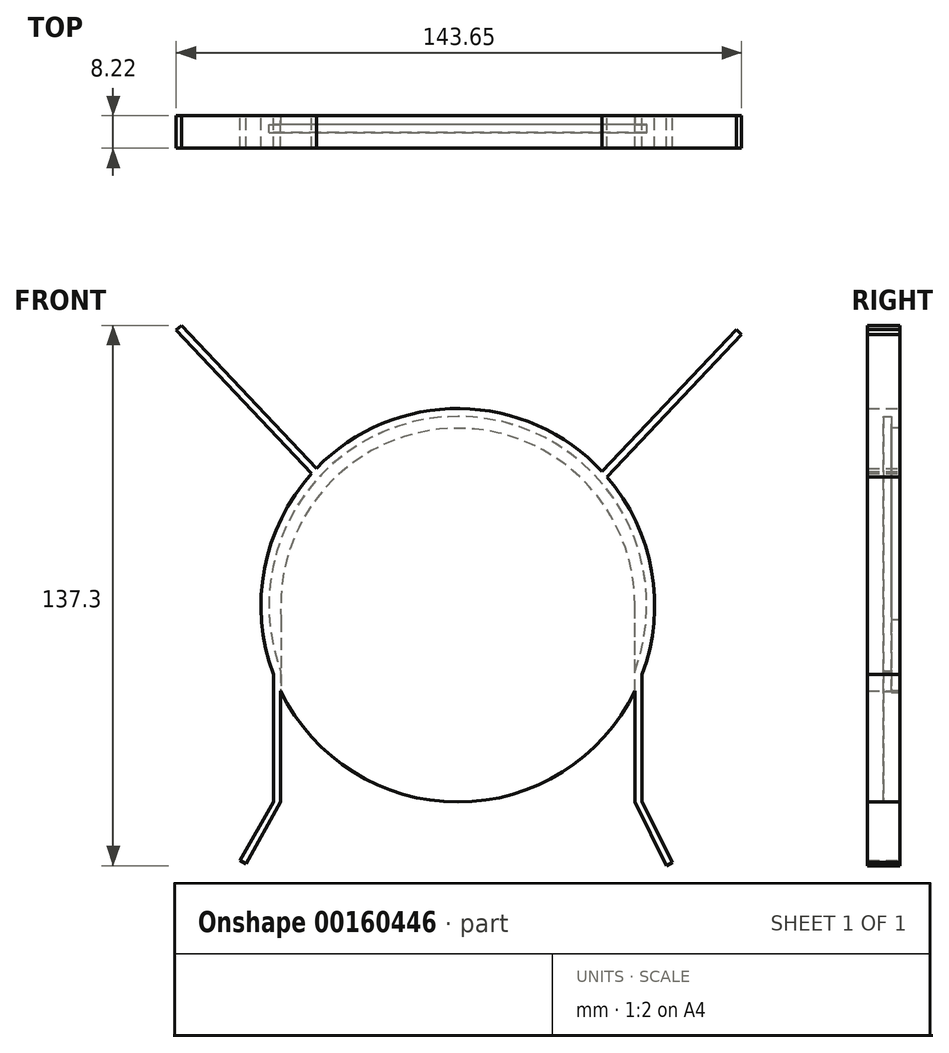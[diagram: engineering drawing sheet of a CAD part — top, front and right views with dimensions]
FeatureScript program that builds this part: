
annotation { "Feature Type Name" : "Feature", "Feature Type Description" : "" }
export const myFeature = defineFeature(function(context is Context, id is Id, definition is map)
    precondition{}
    {
        {
            var Q0;
            Q0=qCreatedBy(makeId("Front.planeOp"),FACE);
            var sketch = newSketch(context, id + "F0", { "sketchPlane" : qUnion([Q0])});
            skLineSegment(sketch, "E0", {"start": v(-45, 0) * mm, "end": v(-45, -50) * mm});
            skLineSegment(sketch, "E1", {"start": v(-45, -50) * mm, "end": v(-46.8, -50) * mm});
            skLineSegment(sketch, "E2", {"start": v(-46.8, -50) * mm, "end": v(-46.8, 0) * mm});
            skLineSegment(sketch, "E3", {"start": v(-46.8, 0) * mm, "end": v(-45, 0) * mm});
            skLineSegment(sketch, "E4", {"start": v(45, 0) * mm, "end": v(45, -50) * mm});
            skLineSegment(sketch, "E5", {"start": v(45, -50) * mm, "end": v(46.8, -50) * mm});
            skLineSegment(sketch, "E6", {"start": v(46.8, -50) * mm, "end": v(46.8, 0) * mm});
            skLineSegment(sketch, "E7", {"start": v(46.8, 0) * mm, "end": v(45, 0) * mm});
            skCircle(sketch, "E8", {"center": v(0, 0) * mm, "radius": 50 * mm});
            skLineSegment(sketch, "E9", {"start": v(-37.12, 33.5) * mm, "end": v(-71.54, 69.91) * mm});
            skLineSegment(sketch, "E10", {"start": v(-71.54, 69.91) * mm, "end": v(-70.23, 71.15) * mm});
            skLineSegment(sketch, "E11", {"start": v(-70.23, 71.15) * mm, "end": v(-35.89, 34.82) * mm});
            skLineSegment(sketch, "E12", {"start": v(36.69, 33.97) * mm, "end": v(70.8, 70.07) * mm});
            skLineSegment(sketch, "E13", {"start": v(70.8, 70.07) * mm, "end": v(72.1, 68.83) * mm});
            skLineSegment(sketch, "E14", {"start": v(72.1, 68.83) * mm, "end": v(37.77, 32.5) * mm});
            skLineSegment(sketch, "E15", {"start": v(-46.8, -50) * mm, "end": v(-55.36, -64.8) * mm});
            skLineSegment(sketch, "E16", {"start": v(-55.36, -64.8) * mm, "end": v(-53.8, -65.7) * mm});
            skLineSegment(sketch, "E17", {"start": v(-53.8, -65.7) * mm, "end": v(-45, -50) * mm});
            skLineSegment(sketch, "E18", {"start": v(45, -50) * mm, "end": v(52.95, -66.15) * mm});
            skLineSegment(sketch, "E19", {"start": v(52.95, -66.15) * mm, "end": v(54.56, -65.36) * mm});
            skLineSegment(sketch, "E20", {"start": v(54.56, -65.36) * mm, "end": v(46.8, -50) * mm});
            skSolve(sketch);
        }
        {
            var Q0;
            Q0=qCreatedBy(makeId("Front.planeOp"),FACE);
            var sketch = newSketch(context, id + "F1", { "sketchPlane" : qUnion([Q0])});
            skSolve(sketch);
        }
        {
            var Q0;
            Q0 = qSketchRegion(id + "F1", true);
            var Q1;
            {var subQ0=sQuery(id+"F0.wireOp",EDGE,"E1");Q1=makeQuery(id+"F0.imprint","IMPRINT",FACE,{"disambiguationData":[TD([[makeQuery(id+"F0.imprint","IMPRINT",EDGE,{"derivedFrom":subQ0}),-1.0]])]});}
            var Q2;
            {var subQ0=sQuery(id+"F0.wireOp",EDGE,"E3");Q2=makeQuery(id+"F0.imprint","IMPRINT",FACE,{"disambiguationData":[TD([[makeQuery(id+"F0.imprint","IMPRINT",EDGE,{"derivedFrom":subQ0}),-1.0]])]});}
            var Q3;
            {var subQ0=sQuery(id+"F0.wireOp",EDGE,"E7");Q3=makeQuery(id+"F0.imprint","IMPRINT",FACE,{"disambiguationData":[TD([[makeQuery(id+"F0.imprint","IMPRINT",EDGE,{"derivedFrom":subQ0}),1.0]])]});}
            var Q4;
            {var subQ0=sQuery(id+"F0.wireOp",EDGE,"E5");Q4=makeQuery(id+"F0.imprint","IMPRINT",FACE,{"disambiguationData":[TD([[makeQuery(id+"F0.imprint","IMPRINT",EDGE,{"derivedFrom":subQ0}),1.0]])]});}
            var Q5;
            {var subQ12=sQuery(id+"F0.wireOp",EDGE,"E3");Q5=makeQuery(id+"F0.imprint","IMPRINT",FACE,{"disambiguationData":[TD([[makeQuery(id+"F0.imprint","IMPRINT",EDGE,{"derivedFrom":subQ12}),1.0]])]});}
            var Q6;
            {var subQ0=sQuery(id+"F0.wireOp",EDGE,"E9");Q6=makeQuery(id+"F0.imprint","IMPRINT",FACE,{"disambiguationData":[TD([[makeQuery(id+"F0.imprint","IMPRINT",EDGE,{"derivedFrom":subQ0}),-1.0]])]});}
            var Q7;
            {var subQ0=sQuery(id+"F0.wireOp",EDGE,"E12");Q7=makeQuery(id+"F0.imprint","IMPRINT",FACE,{"disambiguationData":[TD([[makeQuery(id+"F0.imprint","IMPRINT",EDGE,{"derivedFrom":subQ0}),-1.0]])]});}
            var Q8;
            Q8=makeQuery(id+"F0.imprint","IMPRINT",FACE,{"disambiguationData":[TD([[makeQuery(id+"F0.imprint","IMPRINT",EDGE,{"derivedFrom":sQuery(id+"F0.wireOp",EDGE,"E1")}),1.0]])]});
            var Q9;
            Q9=makeQuery(id+"F0.imprint","IMPRINT",FACE,{"disambiguationData":[TD([[makeQuery(id+"F0.imprint","IMPRINT",EDGE,{"derivedFrom":sQuery(id+"F0.wireOp",EDGE,"E5")}),-1.0]])]});
            extrude(context, id + "F2", {"entities" : qUnion([Q0, Q1, Q2, Q3, Q4, Q5, Q6, Q7, Q8, Q9]), "depth" : 6 * mm});
        }
        {
            var Q0;
            Q0=qCreatedBy(makeId("Front.planeOp"),FACE);
            var sketch = newSketch(context, id + "F3", { "sketchPlane" : qUnion([Q0])});
            skCircle(sketch, "E21", {"center": v(0, 0) * mm, "radius": 48 * mm});
            skSolve(sketch);
        }
        {
            var Q0;
            Q0 = qSketchRegion(id + "F3", true);
            extrude(context, id + "F4", {"entities" : qUnion([Q0]), "operationType" : NewBodyOperationType.REMOVE, "depth" : 2 * mm});
        }
        {
            var Q0;
            Q0=qCreatedBy(makeId("Front.planeOp"),FACE);
            var sketch = newSketch(context, id + "F5", { "sketchPlane" : qUnion([Q0])});
            skLineSegment(sketch, "E22", {"start": v(44.99, -22.07) * mm, "end": v(44.99, -3.86) * mm});
            skLineSegment(sketch, "E23", {"start": v(44.99, -3.86) * mm, "end": v(-45.01, -3.86) * mm});
            skLineSegment(sketch, "E24", {"start": v(-45.01, -3.86) * mm, "end": v(-45.01, -50.71) * mm});
            skLineSegment(sketch, "E25", {"start": v(-45.01, -50.71) * mm, "end": v(44.99, -50.71) * mm});
            skLineSegment(sketch, "E26", {"start": v(44.99, -50.71) * mm, "end": v(44.99, -22.07) * mm});
            skSolve(sketch);
        }
        {
            var Q0;
            Q0=qCreatedBy(makeId("Front.planeOp"),FACE);
            var sketch = newSketch(context, id + "F6", { "sketchPlane" : qUnion([Q0])});
            skSolve(sketch);
        }
        {
            var Q0;
            Q0 = qSketchRegion(id + "F6", true);
            var Q1;
            Q1=makeQuery(id+"F5.imprint","IMPRINT",FACE,{"disambiguationData":[TD([[makeQuery(id+"F5.imprint","IMPRINT",EDGE,{"derivedFrom":sQuery(id+"F5.wireOp",EDGE,"E22")}),1.0]])]});
            extrude(context, id + "F7", {"entities" : qUnion([Q0, Q1]), "operationType" : NewBodyOperationType.REMOVE, "depth" : 2 * mm});
        }
        {
            var Q0;
            Q0=qCreatedBy(makeId("Front.planeOp"),FACE);
            var sketch = newSketch(context, id + "F8", { "sketchPlane" : qUnion([Q0])});
            skCircle(sketch, "E27", {"center": v(0, 0) * mm, "radius": 50 * mm});
            skSolve(sketch);
        }
        {
            var Q0;
            Q0 = qSketchRegion(id + "F8", true);
            extrude(context, id + "F9", {"entities" : qUnion([Q0]), "operationType" : NewBodyOperationType.ADD, "oppositeDirection" : true, "depth" : 2.22 * mm});
        }
        {
            var Q0;
            Q0=qCreatedBy(makeId("Front.planeOp"),FACE);
            var sketch = newSketch(context, id + "F10", { "sketchPlane" : qUnion([Q0])});
            skCircle(sketch, "E28", {"center": v(0, 0) * mm, "radius": 45 * mm});
            skSolve(sketch);
        }
        {
            var Q0;
            Q0 = qSketchRegion(id + "F10", true);
            extrude(context, id + "F11", {"entities" : qUnion([Q0]), "operationType" : NewBodyOperationType.REMOVE, "oppositeDirection" : true, "depth" : 2.22 * mm});
        }
        {
            var Q0;
            {var subQ0=sQuery(id+"F0.wireOp",EDGE,"E11");var subQ1=sQuery(id+"F0.wireOp",EDGE,"E8");var subQ2=sQuery(id+"F0.wireOp",EDGE,"E12");var subQ3=sQuery(id+"F0.wireOp",EDGE,"E6");var subQ4=sQuery(id+"F0.wireOp",EDGE,"E5");var subQ5=sQuery(id+"F0.wireOp",EDGE,"E4");var subQ6=sQuery(id+"F0.wireOp",EDGE,"E9");var subQ7=sQuery(id+"F0.wireOp",EDGE,"E2");var subQ8=sQuery(id+"F0.wireOp",EDGE,"E0");var subQ9=sQuery(id+"F0.wireOp",EDGE,"E14");Q0=makeQuery(id+"F9.boolean.opBoolean","SPLIT",FACE,{"disambiguationData":[TD([makeQuery(id+"F2.opExtrude","SWEPT_FACE",FACE,{"disambiguationData":[OSD([subQ5])]})])],"derivedFrom":makeQuery(id+"F2.opExtrude","CAP_FACE",FACE,{"disambiguationData":[OSD([subQ8,sQuery(id+"F0.wireOp",EDGE,"E1"),subQ7,subQ5,subQ4,subQ3,subQ1,subQ6,sQuery(id+"F0.wireOp",EDGE,"E10"),subQ0,subQ2,sQuery(id+"F0.wireOp",EDGE,"E13"),subQ9])],"isStart":true})});}
            var Q1;
            {var subQ0=sQuery(id+"F0.wireOp",EDGE,"E9");var subQ1=sQuery(id+"F0.wireOp",EDGE,"E8");var subQ2=sQuery(id+"F0.wireOp",EDGE,"E2");var subQ3=sQuery(id+"F0.wireOp",EDGE,"E11");var subQ4=sQuery(id+"F0.wireOp",EDGE,"E12");var subQ6=sQuery(id+"F0.wireOp",EDGE,"E1");var subQ7=sQuery(id+"F0.wireOp",EDGE,"E0");var subQ8=sQuery(id+"F0.wireOp",EDGE,"E4");var subQ9=sQuery(id+"F0.wireOp",EDGE,"E14");var subQ10=sQuery(id+"F0.wireOp",EDGE,"E6");Q1=makeQuery(id+"F9.boolean.opBoolean","SPLIT",FACE,{"disambiguationData":[TD([makeQuery(id+"F2.opExtrude","SWEPT_FACE",FACE,{"disambiguationData":[OSD([subQ6])]})])],"derivedFrom":makeQuery(id+"F2.opExtrude","CAP_FACE",FACE,{"disambiguationData":[OSD([subQ7,subQ6,subQ2,subQ8,sQuery(id+"F0.wireOp",EDGE,"E5"),subQ10,subQ1,subQ0,sQuery(id+"F0.wireOp",EDGE,"E10"),subQ3,subQ4,sQuery(id+"F0.wireOp",EDGE,"E13"),subQ9])],"isStart":true})});}
            extrude(context, id + "F12", {"entities" : qUnion([Q0, Q1]), "operationType" : NewBodyOperationType.ADD, "depth" : 2.22 * mm});
        }
        {
            var Q0;
            Q0=qCreatedBy(makeId("Front.planeOp"),FACE);
            var sketch = newSketch(context, id + "F13", { "sketchPlane" : qUnion([Q0])});
            skLineSegment(sketch, "E29", {"start": v(45, -21.8) * mm, "end": v(45, 0) * mm});
            skLineSegment(sketch, "E30", {"start": v(45, 0) * mm, "end": v(-44.85, 0) * mm});
            skLineSegment(sketch, "E31", {"start": v(-44.85, 0) * mm, "end": v(-44.85, -53.96) * mm});
            skLineSegment(sketch, "E32", {"start": v(-44.85, -53.96) * mm, "end": v(45, -53.96) * mm});
            skLineSegment(sketch, "E33", {"start": v(45, -53.96) * mm, "end": v(45, -21.8) * mm});
            skSolve(sketch);
        }
        {
            var Q0;
            Q0=makeQuery(id+"F13.imprint","IMPRINT",FACE,{"disambiguationData":[TD([[makeQuery(id+"F13.imprint","IMPRINT",EDGE,{"derivedFrom":sQuery(id+"F13.wireOp",EDGE,"E29")}),1.0]])]});
            extrude(context, id + "F14", {"entities" : qUnion([Q0]), "operationType" : NewBodyOperationType.REMOVE, "oppositeDirection" : true, "depth" : 2.22 * mm});
        }
        {
            var Q0;
            {var subQ0=sQuery(id+"F0.wireOp",EDGE,"E16");var subQ1=sQuery(id+"F0.wireOp",EDGE,"E15");var subQ2=sQuery(id+"F0.wireOp",EDGE,"E14");var subQ3=sQuery(id+"F0.wireOp",EDGE,"E8");var subQ4=sQuery(id+"F0.wireOp",EDGE,"E6");var subQ6=sQuery(id+"F0.wireOp",EDGE,"E2");var subQ7=sQuery(id+"F0.wireOp",EDGE,"E17");var subQ8=sQuery(id+"F0.wireOp",EDGE,"E11");var subQ9=sQuery(id+"F0.wireOp",EDGE,"E12");var subQ10=sQuery(id+"F0.wireOp",EDGE,"E9");var subQ11=sQuery(id+"F0.wireOp",EDGE,"E0");var subQ12=sQuery(id+"F0.wireOp",EDGE,"E4");Q0=makeQuery(id+"F9.boolean.opBoolean","SPLIT",FACE,{"disambiguationData":[TD([makeQuery(id+"F2.opExtrude","SWEPT_FACE",FACE,{"disambiguationData":[OSD([subQ6])]})])],"derivedFrom":makeQuery(id+"F2.opExtrude","CAP_FACE",FACE,{"disambiguationData":[OSD([subQ11,subQ6,subQ12,subQ4,subQ3,subQ10,sQuery(id+"F0.wireOp",EDGE,"E10"),subQ8,subQ9,sQuery(id+"F0.wireOp",EDGE,"E13"),subQ2,subQ1,subQ0,subQ7,sQuery(id+"F0.wireOp",EDGE,"E18"),sQuery(id+"F0.wireOp",EDGE,"E19"),sQuery(id+"F0.wireOp",EDGE,"E20")])],"isStart":true})});}
            var Q1;
            {var subQ0=sQuery(id+"F0.wireOp",EDGE,"E14");var subQ1=sQuery(id+"F0.wireOp",EDGE,"E8");var subQ2=sQuery(id+"F0.wireOp",EDGE,"E6");var subQ3=sQuery(id+"F0.wireOp",EDGE,"E0");var subQ4=sQuery(id+"F0.wireOp",EDGE,"E4");var subQ5=sQuery(id+"F0.wireOp",EDGE,"E9");var subQ6=sQuery(id+"F0.wireOp",EDGE,"E2");var subQ7=sQuery(id+"F0.wireOp",EDGE,"E11");var subQ8=sQuery(id+"F0.wireOp",EDGE,"E12");var subQ9=sQuery(id+"F0.wireOp",EDGE,"E10");Q1=makeQuery(id+"F9.boolean.opBoolean","SPLIT",FACE,{"disambiguationData":[TD([makeQuery(id+"F2.opExtrude","SWEPT_FACE",FACE,{"disambiguationData":[OSD([subQ5])]})])],"derivedFrom":makeQuery(id+"F2.opExtrude","CAP_FACE",FACE,{"disambiguationData":[OSD([subQ3,subQ6,subQ4,subQ2,subQ1,subQ5,subQ9,subQ7,subQ8,sQuery(id+"F0.wireOp",EDGE,"E13"),subQ0,sQuery(id+"F0.wireOp",EDGE,"E15"),sQuery(id+"F0.wireOp",EDGE,"E16"),sQuery(id+"F0.wireOp",EDGE,"E17"),sQuery(id+"F0.wireOp",EDGE,"E18"),sQuery(id+"F0.wireOp",EDGE,"E19"),sQuery(id+"F0.wireOp",EDGE,"E20")])],"isStart":true})});}
            var Q2;
            {var subQ0=sQuery(id+"F0.wireOp",EDGE,"E14");var subQ1=sQuery(id+"F0.wireOp",EDGE,"E8");var subQ2=sQuery(id+"F0.wireOp",EDGE,"E6");var subQ3=sQuery(id+"F0.wireOp",EDGE,"E0");var subQ4=sQuery(id+"F0.wireOp",EDGE,"E4");var subQ5=sQuery(id+"F0.wireOp",EDGE,"E9");var subQ6=sQuery(id+"F0.wireOp",EDGE,"E2");var subQ7=sQuery(id+"F0.wireOp",EDGE,"E13");var subQ8=sQuery(id+"F0.wireOp",EDGE,"E11");var subQ9=sQuery(id+"F0.wireOp",EDGE,"E12");Q2=makeQuery(id+"F9.boolean.opBoolean","SPLIT",FACE,{"disambiguationData":[TD([makeQuery(id+"F2.opExtrude","SWEPT_FACE",FACE,{"disambiguationData":[OSD([subQ9])]})])],"derivedFrom":makeQuery(id+"F2.opExtrude","CAP_FACE",FACE,{"disambiguationData":[OSD([subQ3,subQ6,subQ4,subQ2,subQ1,subQ5,sQuery(id+"F0.wireOp",EDGE,"E10"),subQ8,subQ9,subQ7,subQ0,sQuery(id+"F0.wireOp",EDGE,"E15"),sQuery(id+"F0.wireOp",EDGE,"E16"),sQuery(id+"F0.wireOp",EDGE,"E17"),sQuery(id+"F0.wireOp",EDGE,"E18"),sQuery(id+"F0.wireOp",EDGE,"E19"),sQuery(id+"F0.wireOp",EDGE,"E20")])],"isStart":true})});}
            extrude(context, id + "F15", {"entities" : qUnion([Q0, Q1, Q2]), "operationType" : NewBodyOperationType.ADD, "depth" : 2.22 * mm});
        }
    });
